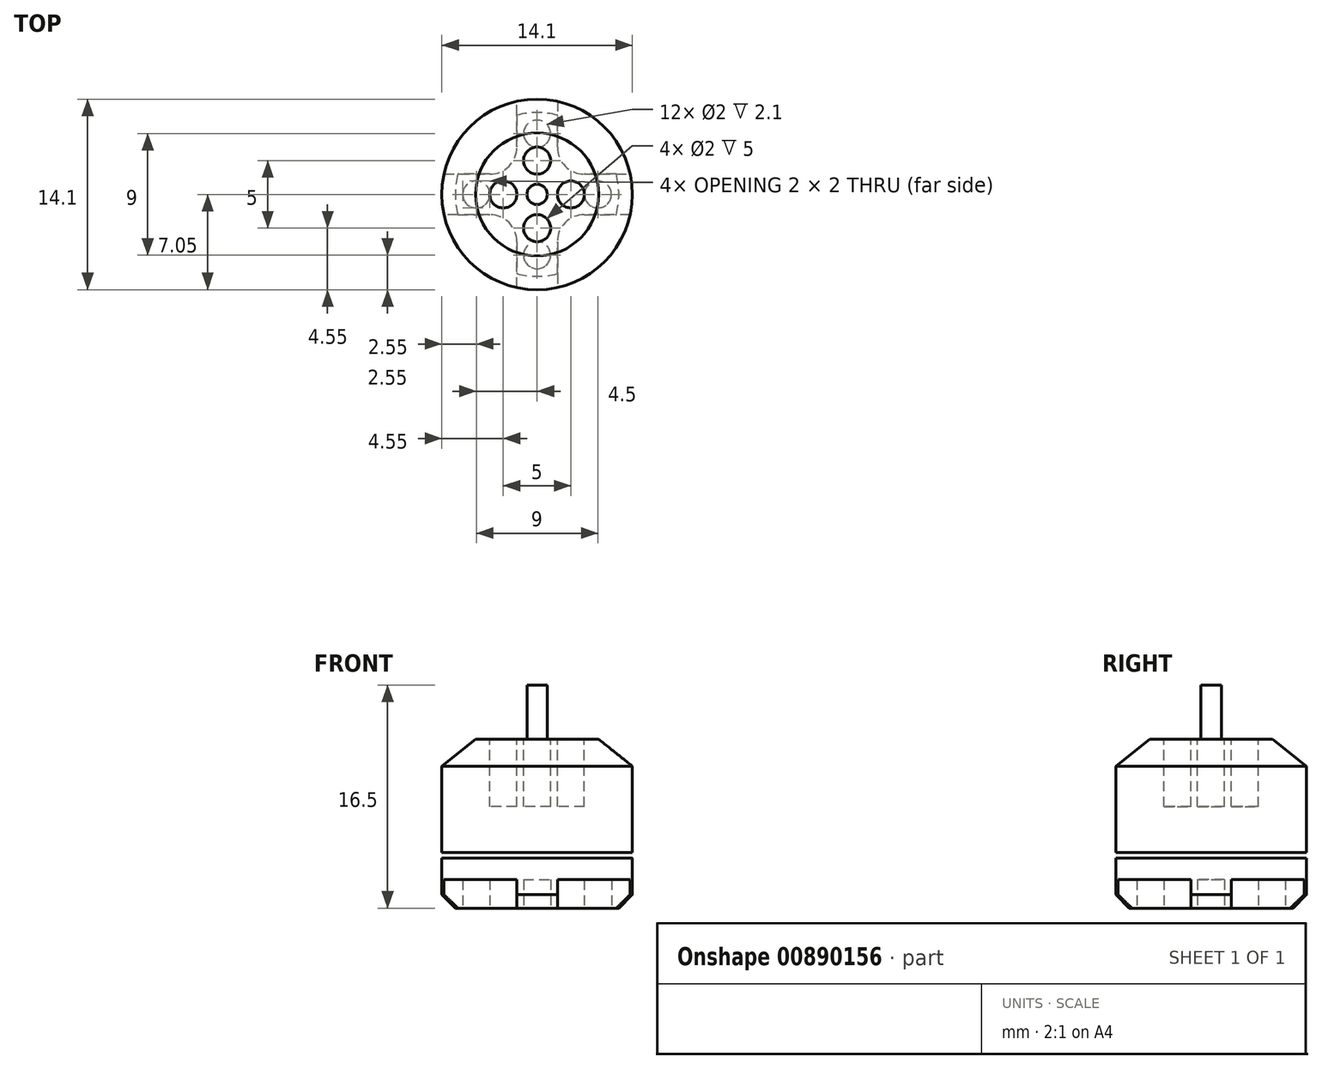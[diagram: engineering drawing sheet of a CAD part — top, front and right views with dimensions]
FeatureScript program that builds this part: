
annotation { "Feature Type Name" : "Feature", "Feature Type Description" : "" }
export const myFeature = defineFeature(function(context is Context, id is Id, definition is map)
    precondition{}
    {
        {
            var Q0;
            Q0=qCreatedBy(makeId("Top.planeOp"),FACE);
            var sketch = newSketch(context, id + "F0", { "sketchPlane" : qUnion([Q0])});
            skCircle(sketch, "E0", {"center": v(0, 0) * mm, "radius": 7.05 * mm});
            skCircle(sketch, "E1", {"center": v(0, 0) * mm, "radius": 0.75 * mm});
            skCircle(sketch, "E2", {"center": v(0, 0) * mm, "radius": 2.5 * mm, "construction": true});
            skCircle(sketch, "E3", {"center": v(0, 0) * mm, "radius": 4.5 * mm});
            skCircle(sketch, "E4", {"center": v(2.5, 0) * mm, "radius": 1 * mm});
            skCircle(sketch, "E5.1.0", {"center": v(0, 2.5) * mm, "radius": 1 * mm});
            skCircle(sketch, "E5.2.0", {"center": v(-2.5, 0) * mm, "radius": 1 * mm});
            skCircle(sketch, "E5.3.0", {"center": v(0, -2.5) * mm, "radius": 1 * mm});
            skSolve(sketch);
        }
        {
            var Q0;
            Q0=makeQuery(id+"F0.imprint","IMPRINT",FACE,{"disambiguationData":[TD([[makeQuery(id+"F0.imprint","IMPRINT",EDGE,{"derivedFrom":sQuery(id+"F0.wireOp",EDGE,"E0")}),1.0]])]});
            var Q1;
            {var subQ0=sQuery(id+"F0.wireOp",EDGE,"E5.1.0");var subQ1=sQuery(id+"F0.wireOp",EDGE,"E2");var subQ2=makeQuery(id+"F0.imprint","INTERSECT",VERTEX,{"derivedFrom":[subQ1,subQ0]});Q1=makeQuery(id+"F0.imprint","IMPRINT",FACE,{"disambiguationData":[TD([[makeQuery(id+"F0.imprint","IMPRINT",EDGE,{"disambiguationData":[TD([[subQ2,1.0]])],"derivedFrom":subQ1}),-1.0]])]});}
            var Q2;
            {var subQ0=sQuery(id+"F0.wireOp",EDGE,"E5.1.0");var subQ1=sQuery(id+"F0.wireOp",EDGE,"E2");var subQ2=makeQuery(id+"F0.imprint","INTERSECT",VERTEX,{"derivedFrom":[subQ1,subQ0]});Q2=makeQuery(id+"F0.imprint","IMPRINT",FACE,{"disambiguationData":[TD([[makeQuery(id+"F0.imprint","IMPRINT",EDGE,{"disambiguationData":[TD([[subQ2,-1.0]])],"derivedFrom":subQ1}),-1.0]])]});}
            var Q3;
            Q3=makeQuery(id+"F0.imprint","IMPRINT",FACE,{"disambiguationData":[TD([[makeQuery(id+"F0.imprint","IMPRINT",EDGE,{"derivedFrom":sQuery(id+"F0.wireOp",EDGE,"E1")}),-1.0]])]});
            var Q4;
            {var subQ0=sQuery(id+"F0.wireOp",EDGE,"E4");var subQ1=sQuery(id+"F0.wireOp",EDGE,"E2");var subQ2=makeQuery(id+"F0.imprint","INTERSECT",VERTEX,{"derivedFrom":[subQ1,subQ0]});Q4=makeQuery(id+"F0.imprint","IMPRINT",FACE,{"disambiguationData":[TD([[makeQuery(id+"F0.imprint","IMPRINT",EDGE,{"disambiguationData":[TD([[subQ2,1.0]])],"derivedFrom":subQ1}),-1.0]])]});}
            var Q5;
            {var subQ0=sQuery(id+"F0.wireOp",EDGE,"E5.2.0");var subQ1=sQuery(id+"F0.wireOp",EDGE,"E2");var subQ2=makeQuery(id+"F0.imprint","INTERSECT",VERTEX,{"derivedFrom":[subQ1,subQ0]});Q5=makeQuery(id+"F0.imprint","IMPRINT",FACE,{"disambiguationData":[TD([[makeQuery(id+"F0.imprint","IMPRINT",EDGE,{"disambiguationData":[TD([[subQ2,-1.0]])],"derivedFrom":subQ1}),-1.0]])]});}
            var Q6;
            Q6=makeQuery(id+"F0.imprint","IMPRINT",FACE,{"disambiguationData":[TD([[makeQuery(id+"F0.imprint","IMPRINT",EDGE,{"derivedFrom":sQuery(id+"F0.wireOp",EDGE,"E1")}),1.0]])]});
            var Q7;
            {var subQ0=sQuery(id+"F0.wireOp",EDGE,"E5.2.0");var subQ1=sQuery(id+"F0.wireOp",EDGE,"E3");var subQ2=makeQuery(id+"F0.imprint","INTERSECT",VERTEX,{"disambiguationData":[OD(0.0)],"derivedFrom":[subQ1,subQ0]});Q7=makeQuery(id+"F0.imprint","IMPRINT",FACE,{"disambiguationData":[TD([[makeQuery(id+"F0.imprint","IMPRINT",EDGE,{"disambiguationData":[TD([[subQ2,-1.0]])],"derivedFrom":subQ1}),-1.0]])]});}
            var Q8;
            {var subQ0=sQuery(id+"F0.wireOp",EDGE,"E5.2.0");var subQ1=sQuery(id+"F0.wireOp",EDGE,"E3");var subQ2=makeQuery(id+"F0.imprint","INTERSECT",VERTEX,{"disambiguationData":[OD(0.0)],"derivedFrom":[subQ1,subQ0]});Q8=makeQuery(id+"F0.imprint","IMPRINT",FACE,{"disambiguationData":[TD([[makeQuery(id+"F0.imprint","IMPRINT",EDGE,{"disambiguationData":[TD([[subQ2,-1.0]])],"derivedFrom":subQ1}),1.0]])]});}
            var Q9;
            {var subQ0=sQuery(id+"F0.wireOp",EDGE,"E5.1.0");var subQ1=sQuery(id+"F0.wireOp",EDGE,"E3");var subQ2=makeQuery(id+"F0.imprint","INTERSECT",VERTEX,{"disambiguationData":[OD(0.0)],"derivedFrom":[subQ1,subQ0]});Q9=makeQuery(id+"F0.imprint","IMPRINT",FACE,{"disambiguationData":[TD([[makeQuery(id+"F0.imprint","IMPRINT",EDGE,{"disambiguationData":[TD([[subQ2,-1.0]])],"derivedFrom":subQ1}),1.0]])]});}
            var Q10;
            {var subQ0=sQuery(id+"F0.wireOp",EDGE,"E4");var subQ1=sQuery(id+"F0.wireOp",EDGE,"E3");var subQ2=makeQuery(id+"F0.imprint","INTERSECT",VERTEX,{"disambiguationData":[OD(0.0)],"derivedFrom":[subQ1,subQ0]});Q10=makeQuery(id+"F0.imprint","IMPRINT",FACE,{"disambiguationData":[TD([[makeQuery(id+"F0.imprint","IMPRINT",EDGE,{"disambiguationData":[TD([[subQ2,1.0]])],"derivedFrom":subQ1}),1.0]])]});}
            var Q11;
            {var subQ0=sQuery(id+"F0.wireOp",EDGE,"E4");var subQ1=sQuery(id+"F0.wireOp",EDGE,"E3");var subQ2=makeQuery(id+"F0.imprint","INTERSECT",VERTEX,{"disambiguationData":[OD(0.0)],"derivedFrom":[subQ1,subQ0]});Q11=makeQuery(id+"F0.imprint","IMPRINT",FACE,{"disambiguationData":[TD([[makeQuery(id+"F0.imprint","IMPRINT",EDGE,{"disambiguationData":[TD([[subQ2,1.0]])],"derivedFrom":subQ1}),-1.0]])]});}
            var Q12;
            {var subQ0=sQuery(id+"F0.wireOp",EDGE,"E5.3.0");var subQ1=sQuery(id+"F0.wireOp",EDGE,"E3");var subQ2=makeQuery(id+"F0.imprint","INTERSECT",VERTEX,{"disambiguationData":[OD(0.0)],"derivedFrom":[subQ1,subQ0]});Q12=makeQuery(id+"F0.imprint","IMPRINT",FACE,{"disambiguationData":[TD([[makeQuery(id+"F0.imprint","IMPRINT",EDGE,{"disambiguationData":[TD([[subQ2,-1.0]])],"derivedFrom":subQ1}),1.0]])]});}
            var Q13;
            {var subQ0=sQuery(id+"F0.wireOp",EDGE,"E5.1.0");var subQ1=sQuery(id+"F0.wireOp",EDGE,"E3");var subQ2=makeQuery(id+"F0.imprint","INTERSECT",VERTEX,{"disambiguationData":[OD(0.0)],"derivedFrom":[subQ1,subQ0]});Q13=makeQuery(id+"F0.imprint","IMPRINT",FACE,{"disambiguationData":[TD([[makeQuery(id+"F0.imprint","IMPRINT",EDGE,{"disambiguationData":[TD([[subQ2,-1.0]])],"derivedFrom":subQ1}),-1.0]])]});}
            var Q14;
            {var subQ0=sQuery(id+"F0.wireOp",EDGE,"E5.3.0");var subQ1=sQuery(id+"F0.wireOp",EDGE,"E3");var subQ2=makeQuery(id+"F0.imprint","INTERSECT",VERTEX,{"disambiguationData":[OD(0.0)],"derivedFrom":[subQ1,subQ0]});Q14=makeQuery(id+"F0.imprint","IMPRINT",FACE,{"disambiguationData":[TD([[makeQuery(id+"F0.imprint","IMPRINT",EDGE,{"disambiguationData":[TD([[subQ2,-1.0]])],"derivedFrom":subQ1}),-1.0]])]});}
            var Q15;
            Q15=makeQuery(id+"F0.imprint","IMPRINT",FACE,{"disambiguationData":[TD([[makeQuery(id+"F0.imprint","IMPRINT",EDGE,{"derivedFrom":sQuery(id+"F0.wireOp",EDGE,"E5.3.0")}),1.0]])]});
            var Q16;
            Q16=makeQuery(id+"F0.imprint","IMPRINT",FACE,{"disambiguationData":[TD([[makeQuery(id+"F0.imprint","IMPRINT",EDGE,{"derivedFrom":sQuery(id+"F0.wireOp",EDGE,"E4")}),1.0]])]});
            var Q17;
            Q17=makeQuery(id+"F0.imprint","IMPRINT",FACE,{"disambiguationData":[TD([[makeQuery(id+"F0.imprint","IMPRINT",EDGE,{"derivedFrom":sQuery(id+"F0.wireOp",EDGE,"E5.1.0")}),1.0]])]});
            var Q18;
            Q18=makeQuery(id+"F0.imprint","IMPRINT",FACE,{"disambiguationData":[TD([[makeQuery(id+"F0.imprint","IMPRINT",EDGE,{"derivedFrom":sQuery(id+"F0.wireOp",EDGE,"E5.2.0")}),1.0]])]});
            extrude(context, id + "F1", {"entities" : qUnion([Q0, Q1, Q2, Q3, Q4, Q5, Q6, Q7, Q8, Q9, Q10, Q11, Q12, Q13, Q14, Q15, Q16, Q17, Q18]), "oppositeDirection" : true, "offsetDistance" : 25 * mm, "depth" : 12.5 * mm});
        }
        {
            var Q0;
            Q0=makeQuery(id+"F1.opExtrude","CAP_EDGE",EDGE,{"disambiguationData":[OSD([sQuery(id+"F0.wireOp",EDGE,"E0")])],"isStart":true});
            chamfer(context, id + "F2", {"entities" : qUnion([Q0]), "chamferType" : ChamferType.TWO_OFFSETS, "width1" : 2.5 * mm, "oppositeDirection" : false, "width2" : 2 * mm, "tangentPropagation" : true});
        }
        {
            var Q0;
            Q0=makeQuery(id+"F0.imprint","IMPRINT",FACE,{"disambiguationData":[TD([[makeQuery(id+"F0.imprint","IMPRINT",EDGE,{"derivedFrom":sQuery(id+"F0.wireOp",EDGE,"E1")}),1.0]])]});
            var Q1;
            Q1=sQuery(id+"F0.wireOp",EDGE,"E1");
            extrude(context, id + "F3", {"entities" : qUnion([Q0]), "operationType" : NewBodyOperationType.ADD, "surfaceEntities" : qUnion([Q1]), "offsetDistance" : 25 * mm, "depth" : 4 * mm});
        }
        {
            var Q0;
            Q0=makeQuery(id+"F0.imprint","IMPRINT",FACE,{"disambiguationData":[TD([[makeQuery(id+"F0.imprint","IMPRINT",EDGE,{"derivedFrom":sQuery(id+"F0.wireOp",EDGE,"E5.2.0")}),1.0]])]});
            var Q1;
            Q1=makeQuery(id+"F0.imprint","IMPRINT",FACE,{"disambiguationData":[TD([[makeQuery(id+"F0.imprint","IMPRINT",EDGE,{"derivedFrom":sQuery(id+"F0.wireOp",EDGE,"E4")}),1.0]])]});
            var Q2;
            Q2=makeQuery(id+"F0.imprint","IMPRINT",FACE,{"disambiguationData":[TD([[makeQuery(id+"F0.imprint","IMPRINT",EDGE,{"derivedFrom":sQuery(id+"F0.wireOp",EDGE,"E5.1.0")}),1.0]])]});
            var Q3;
            Q3=makeQuery(id+"F0.imprint","IMPRINT",FACE,{"disambiguationData":[TD([[makeQuery(id+"F0.imprint","IMPRINT",EDGE,{"derivedFrom":sQuery(id+"F0.wireOp",EDGE,"E5.3.0")}),1.0]])]});
            var Q4;
            Q4=sQuery(id+"F0.wireOp",EDGE,"E4");
            extrude(context, id + "F4", {"entities" : qUnion([Q0, Q1, Q2, Q3]), "operationType" : NewBodyOperationType.REMOVE, "surfaceEntities" : qUnion([Q4]), "oppositeDirection" : true, "depth" : 5 * mm, "offsetDistance" : 25 * mm});
        }
        {
            var Q0;
            Q0=makeQuery(id+"F1.opExtrude","CAP_EDGE",EDGE,{"disambiguationData":[OSD([sQuery(id+"F0.wireOp",EDGE,"E0")])],"isStart":false});
            chamfer(context, id + "F5", {"entities" : qUnion([Q0]), "width" : 1 * mm, "tangentPropagation" : true});
        }
        {
            var Q0;
            Q0=makeQuery(id+"F1.opExtrude","CAP_FACE",FACE,{"disambiguationData":[OSD([sQuery(id+"F0.wireOp",EDGE,"E0")])],"isStart":false});
            cPlane(context, id + "F6", {"entities" : qUnion([Q0]), "cplaneType" : CPlaneType.OFFSET, "offset" : .4 * mm, "width" : 150 * mm, "height" : 150 * mm});
        }
        {
            var Q0;
            Q0=qCreatedBy(id+"F6.planeOp",FACE);
            var sketch = newSketch(context, id + "F7", { "sketchPlane" : qUnion([Q0])});
            skCircle(sketch, "E6", {"center": v(0, 0) * mm, "radius": 4.5 * mm, "construction": true});
            skCircle(sketch, "E7", {"center": v(4.5, 0) * mm, "radius": 1 * mm});
            skCircle(sketch, "E8.1.0", {"center": v(0, 4.5) * mm, "radius": 1 * mm});
            skCircle(sketch, "E8.2.0", {"center": v(-4.5, 0) * mm, "radius": 1 * mm});
            skCircle(sketch, "E8.3.0", {"center": v(0, -4.5) * mm, "radius": 1 * mm});
            skLineSegment(sketch, "E9", {"start": v(3.5, -1.5) * mm, "end": v(12.57, -1.5) * mm});
            skLineSegment(sketch, "E10", {"start": v(12.57, -1.5) * mm, "end": v(1.5, -12.57) * mm});
            skLineSegment(sketch, "E11", {"start": v(1.5, -12.57) * mm, "end": v(1.5, -3.5) * mm});
            skArc(sketch, "E12", {"start": v(3.5, -1.5) * mm, "mid": v(2.09, -2.09) * mm, "end": v(1.5, -3.5) * mm});
            skLineSegment(sketch, "E13.1.0", {"start": v(1.5, 12.57) * mm, "end": v(12.57, 1.5) * mm});
            skLineSegment(sketch, "E13.1.1", {"start": v(1.5, 3.5) * mm, "end": v(1.5, 12.57) * mm});
            skArc(sketch, "E13.1.2", {"start": v(1.5, 3.5) * mm, "mid": v(2.09, 2.09) * mm, "end": v(3.5, 1.5) * mm});
            skLineSegment(sketch, "E13.1.3", {"start": v(12.57, 1.5) * mm, "end": v(3.5, 1.5) * mm});
            skLineSegment(sketch, "E13.2.0", {"start": v(-12.57, 1.5) * mm, "end": v(-1.5, 12.57) * mm});
            skLineSegment(sketch, "E13.2.1", {"start": v(-3.5, 1.5) * mm, "end": v(-12.57, 1.5) * mm});
            skArc(sketch, "E13.2.2", {"start": v(-3.5, 1.5) * mm, "mid": v(-2.09, 2.09) * mm, "end": v(-1.5, 3.5) * mm});
            skLineSegment(sketch, "E13.2.3", {"start": v(-1.5, 12.57) * mm, "end": v(-1.5, 3.5) * mm});
            skLineSegment(sketch, "E13.3.0", {"start": v(-1.5, -12.57) * mm, "end": v(-12.57, -1.5) * mm});
            skLineSegment(sketch, "E13.3.1", {"start": v(-1.5, -3.5) * mm, "end": v(-1.5, -12.57) * mm});
            skArc(sketch, "E13.3.2", {"start": v(-1.5, -3.5) * mm, "mid": v(-2.09, -2.09) * mm, "end": v(-3.5, -1.5) * mm});
            skLineSegment(sketch, "E13.3.3", {"start": v(-12.57, -1.5) * mm, "end": v(-3.5, -1.5) * mm});
            skSolve(sketch);
        }
        {
            var Q0;
            Q0 = qSketchRegion(id + "F7", true);
            extrude(context, id + "F8", {"entities" : qUnion([Q0]), "operationType" : NewBodyOperationType.REMOVE, "oppositeDirection" : true, "depth" : 2.5 * mm, "offsetDistance" : 25 * mm});
        }
        {
            var Q0;
            Q0=makeQuery(id+"F1.opExtrude","CAP_FACE",FACE,{"disambiguationData":[OSD([sQuery(id+"F0.wireOp",EDGE,"E0")])],"isStart":false});
            cPlane(context, id + "F9", {"entities" : qUnion([Q0]), "cplaneType" : CPlaneType.OFFSET, "offset" : 3.7 * mm, "oppositeDirection" : true, "width" : 150 * mm, "height" : 150 * mm});
        }
        {
            var Q0;
            Q0=qCreatedBy(id+"F9.planeOp",FACE);
            var sketch = newSketch(context, id + "F10", { "sketchPlane" : qUnion([Q0])});
            skCircle(sketch, "E14", {"center": v(0, 0) * mm, "radius": 8.05 * mm});
            skSolve(sketch);
        }
        {
            var Q0;
            Q0=makeQuery(id+"F10.imprint","IMPRINT",FACE,{"disambiguationData":[TD([[makeQuery(id+"F10.imprint","IMPRINT",EDGE,{"derivedFrom":sQuery(id+"F10.wireOp",EDGE,"E14")}),1.0]])]});
            extrude(context, id + "F11", {"entities" : qUnion([Q0]), "operationType" : NewBodyOperationType.REMOVE, "oppositeDirection" : true, "depth" : .4 * mm, "offsetDistance" : 25 * mm});
        }
    });
